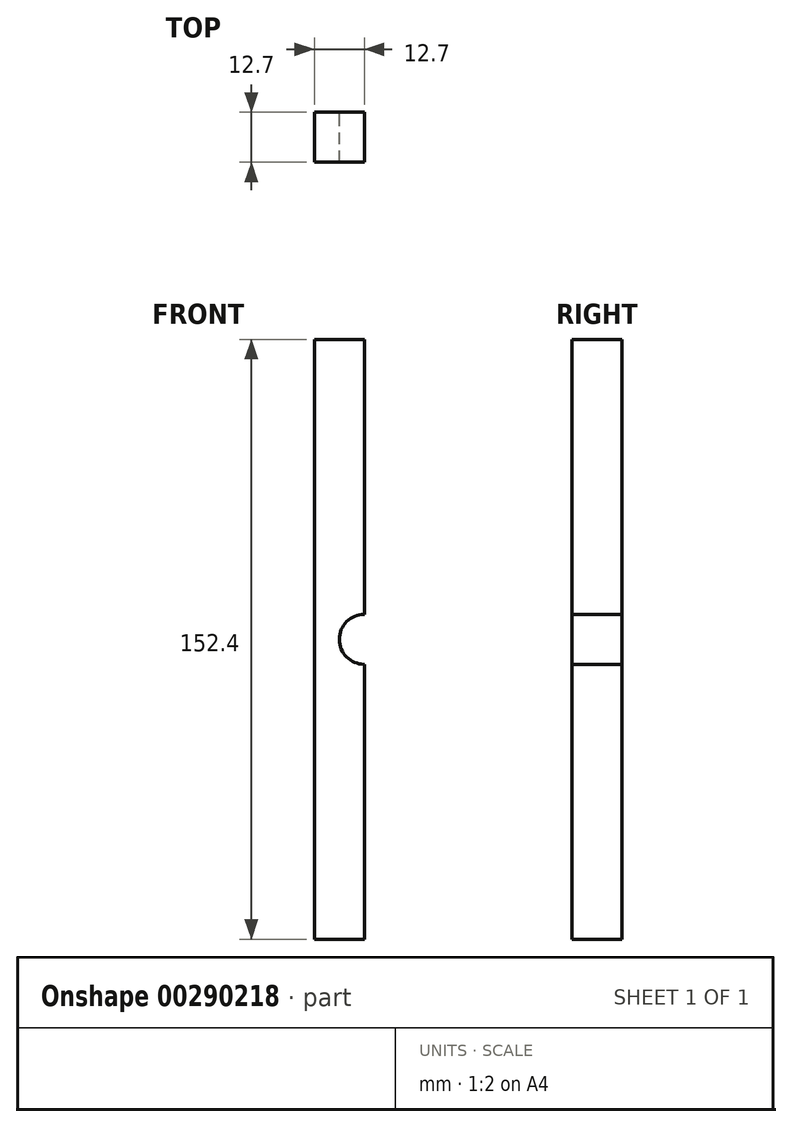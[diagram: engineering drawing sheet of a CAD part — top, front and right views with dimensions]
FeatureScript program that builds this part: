
annotation { "Feature Type Name" : "Feature", "Feature Type Description" : "" }
export const myFeature = defineFeature(function(context is Context, id is Id, definition is map)
    precondition{}
    {
        {
            var Q0;
            Q0=qCreatedBy(makeId("Front.planeOp"),FACE);
            var sketch = newSketch(context, id + "F0", { "sketchPlane" : qUnion([Q0])});
            skLineSegment(sketch, "E0", {"start": v(0, 0) * mm, "end": v(-12.7, 0) * mm});
            skLineSegment(sketch, "E1", {"start": v(-12.7, 0) * mm, "end": v(-12.7, 152.4) * mm});
            skLineSegment(sketch, "E2", {"start": v(-12.7, 152.4) * mm, "end": v(0, 152.4) * mm});
            skLineSegment(sketch, "E3", {"start": v(0, 152.4) * mm, "end": v(0, 82.55) * mm});
            skArc(sketch, "E4", {"start": v(0, 82.55) * mm, "mid": v(-6.35, 76.2) * mm, "end": v(0, 69.85) * mm});
            skLineSegment(sketch, "E5.trimOffspring", {"start": v(0, 69.85) * mm, "end": v(0, 0) * mm});
            skSolve(sketch);
        }
        {
            var Q0;
            Q0=makeQuery(id+"F0.imprint","IMPRINT",FACE,{"disambiguationData":[TD([[makeQuery(id+"F0.imprint","IMPRINT",EDGE,{"derivedFrom":sQuery(id+"F0.wireOp",EDGE,"E0")}),-1.0]])]});
            extrude(context, id + "F1", {"entities" : qUnion([Q0]), "depth" : 12.7 * mm});
        }
    });
